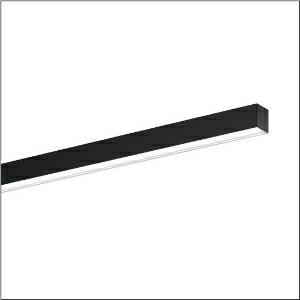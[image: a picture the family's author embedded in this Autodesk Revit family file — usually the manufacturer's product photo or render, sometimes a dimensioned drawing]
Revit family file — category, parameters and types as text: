
# Revit family: silica_r__21_51mx20tct5b_b82d
name_source: partatom
category: Lighting Fixtures
units: mm (PartAtom-declared; Revit-internal decimal feet)

## family parameters
Cut with Voids When Loaded = No
Host = Face
Light Source = No
Part Type = Normal
Room Calculation Point = No
Round Connector Dimension = Use Diameter
Shared = No

## types (1)
- --- (1 x LED, 6000 lm, 51.3 W, 6500K)
    Apparent Load = 51 VA
    CIE Flux Codes = 48 79 96 100 100
    Color Rendering = 80
    Color Temperature = 6500K
    Default Elevation = 1800 mm
    Description = Silica® 21, office luminaire, primary optical cover: cover, of PMMA, opal, light emission: direct distribution, primary light characteristic: symmetric, installation type: surface-mounted, LED, rated luminous flux: 6.000lm, luminous efficacy: 112lm/W, light colour: 8tw, colour temperature: 2700..6500K, control gear: DALI DT8, with terminal, 3+2-pole, max. 2.5mm², mains connection: 220..240V, AC, 50/60Hz, rated input power: 53.8W, luminaire housing, of aluminium, matt jet black (RAL 9005), length: 3.004mm, width: 53mm, height: 53mm, protection rating (complete): IP20, insulation class (complete): insulation class I (protective earthing), certification: CE, permissible operating ambient temperature: 0..+35°C, standard: EN 50419, packaging unit: 1 piece
    Height = 53 mm
    Lamp = 1 x LED
    Lamp Light Flux = 6000 lm
    Lamp Power = 51.3 W
    Lamp count = 1
    Length = 3004 mm
    Luminous efficacy = 117 lm/W
    Manufacturer = Siteco
    ModVariant = No
    Model = 51MX20TCT5B
    Mounting Place = Ceiling
    Mounting Type = Surface mounted
    Number of Poles = 1
    OnlyDefault = Yes
    Power Factor = 1
    Product Name = Silica® 21
    Product group = office luminaire | ceiling mounted
    ProductGroupID = 302
    Protection Class = Protection class I
    Protection Degree = IP 20
    RLX_Detail_Level = 1
    RLX_Emergency_Light_Flux = 0 lm
    RLX_Emergency_Type = 0
    RLX_Emergency_Type_DB = No
    RlxData = <blob elided: 25565 chars, md5=6c1454b9>
    Socket = socket
    Standby Power = 0 W
    System Light Flux = 6000 lm
    System Power = 51 W
    Type Comments = individual setting
    Type Image = l_1335925.jpg
    URL = http://relux.com
    VarID = @adj_139680
    Voltage = 0 V
    Weight = 0.00 kg
    Width = 53 mm

## geometry (parser evidence)
native form markers: Blend x4, Sweep x10
no freeform markers — native parametric forms only
